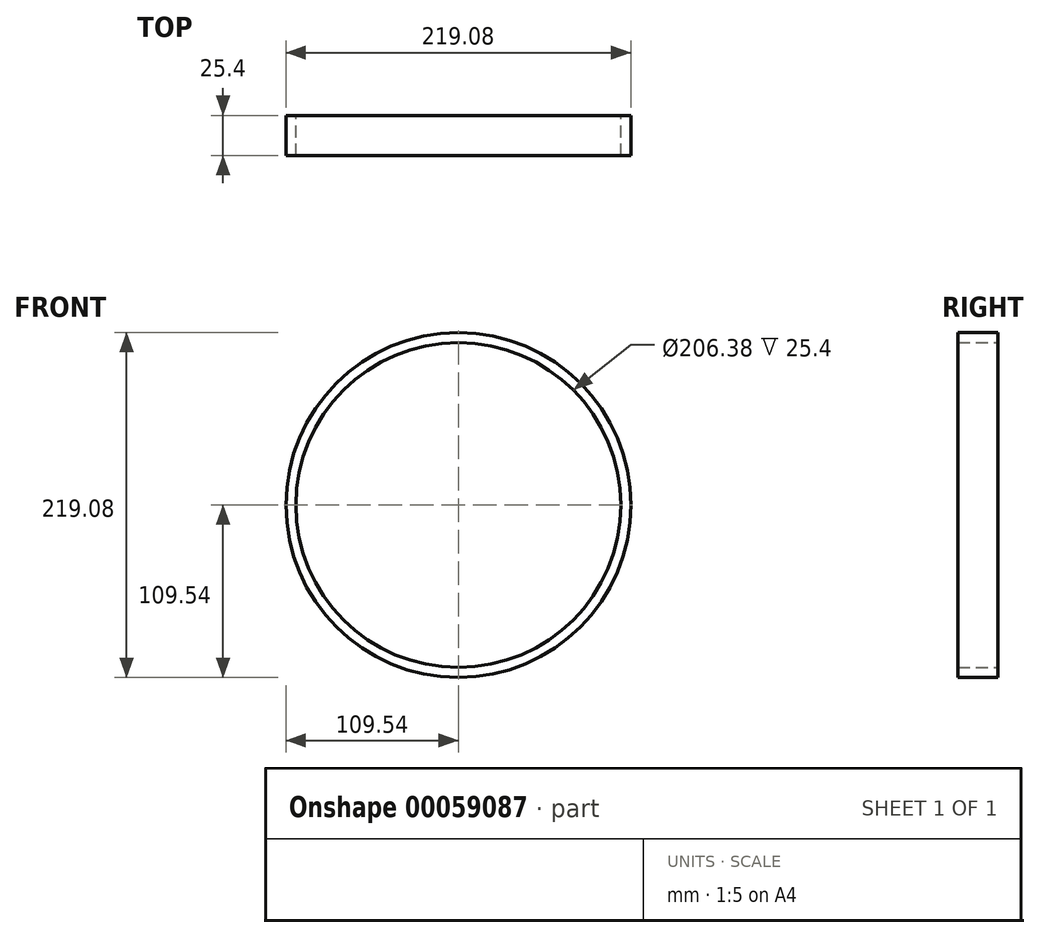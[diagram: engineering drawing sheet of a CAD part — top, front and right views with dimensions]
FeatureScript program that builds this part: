
annotation { "Feature Type Name" : "Feature", "Feature Type Description" : "" }
export const myFeature = defineFeature(function(context is Context, id is Id, definition is map)
    precondition{}
    {
        {
            var Q0;
            Q0=qCreatedBy(makeId("Front.planeOp"),FACE);
            var sketch = newSketch(context, id + "F0", { "sketchPlane" : qUnion([Q0])});
            skCircle(sketch, "E0", {"center": v(0, 0) * mm, "radius": 109.54 * mm});
            skCircle(sketch, "E1.0", {"center": v(0, 0) * mm, "radius": 103.19 * mm});
            skSolve(sketch);
        }
        {
            var Q0;
            Q0 = qSketchRegion(id + "F0", true);
            extrude(context, id + "F1", {"entities" : qUnion([Q0]), "depth" : 25.4 * mm});
        }
    });
